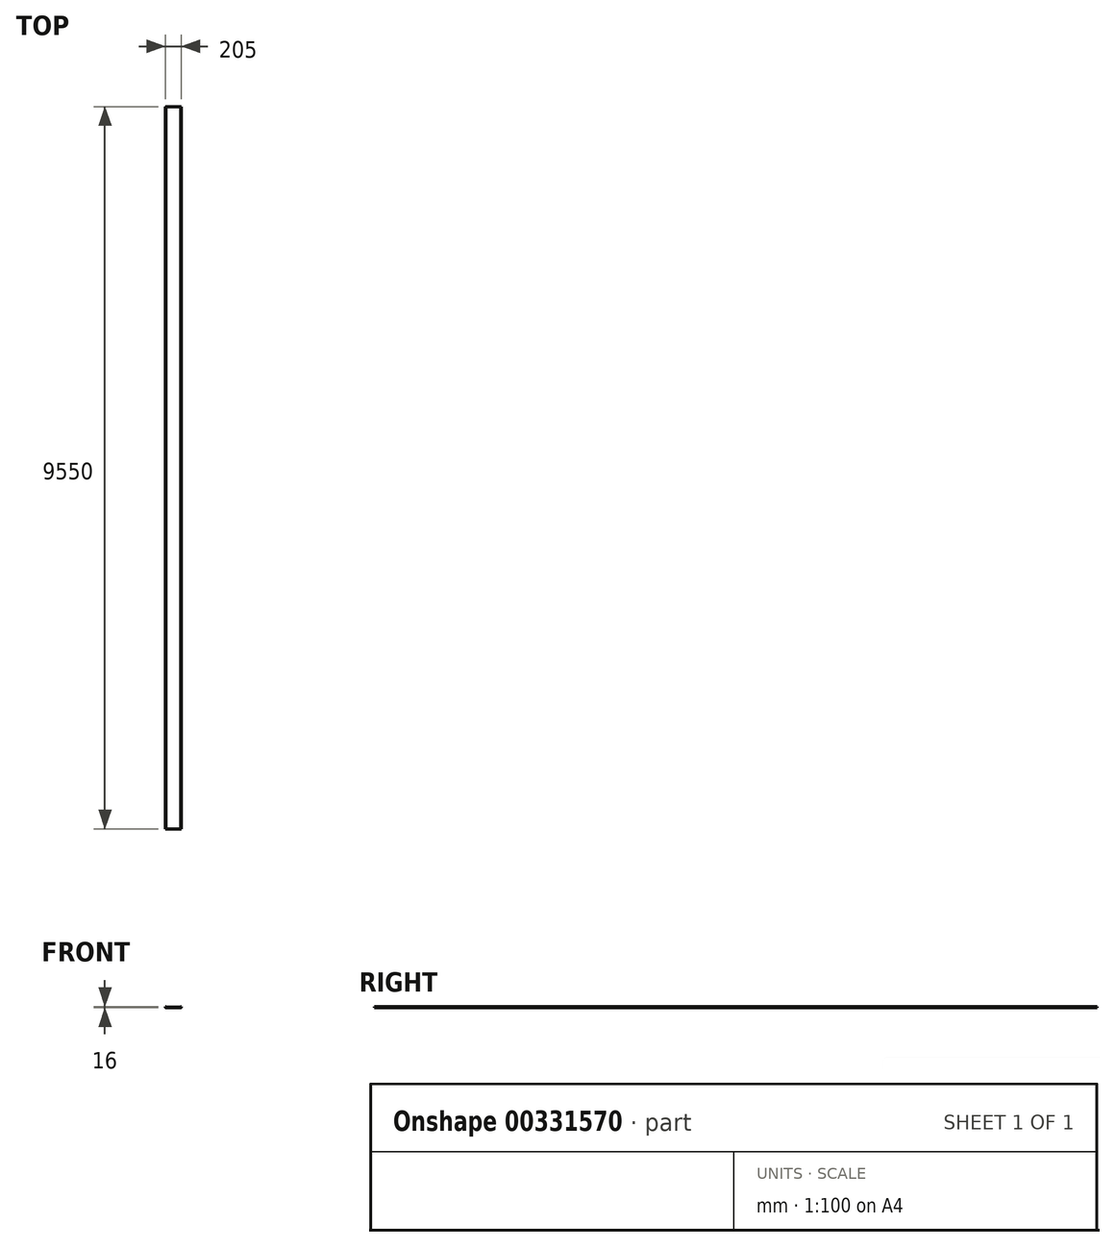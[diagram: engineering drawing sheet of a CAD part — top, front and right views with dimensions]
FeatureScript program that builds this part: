
annotation { "Feature Type Name" : "Feature", "Feature Type Description" : "" }
export const myFeature = defineFeature(function(context is Context, id is Id, definition is map)
    precondition{}
    {
        {
            var Q0;
            Q0=qCreatedBy(makeId("Front.planeOp"),FACE);
            var sketch = newSketch(context, id + "F0", { "sketchPlane" : qUnion([Q0])});
            skLineSegment(sketch, "E0.top", {"start": v(100, -16) * mm, "end": v(-100, -16) * mm});
            skLineSegment(sketch, "E0.left", {"start": v(102.5, 0) * mm, "end": v(102.5, -13.5) * mm});
            skLineSegment(sketch, "E0.right", {"start": v(-102.5, 0) * mm, "end": v(-102.5, -13.5) * mm});
            skPoint(sketch, "E0.middle", {"position": v(0, 0) * mm});
            skLineSegment(sketch, "E1.bottom", {"start": v(94, -10) * mm, "end": v(-94, -10) * mm});
            skLineSegment(sketch, "E1.left", {"start": v(96.5, -7.5) * mm, "end": v(96.5, 0) * mm});
            skLineSegment(sketch, "E1.right", {"start": v(-96.5, -7.5) * mm, "end": v(-96.5, 0) * mm});
            skLineSegment(sketch, "E2.bottom", {"start": v(97, -13) * mm, "end": v(-97, -13) * mm});
            skLineSegment(sketch, "E2.left", {"start": v(99.5, -10.5) * mm, "end": v(99.5, 0) * mm});
            skLineSegment(sketch, "E2.right", {"start": v(-99.5, -10.5) * mm, "end": v(-99.5, 0) * mm});
            skLineSegment(sketch, "E3", {"start": v(-102.5, 0) * mm, "end": v(-96.5, 0) * mm});
            skPoint(sketch, "E4.orphan", {"position": v(-99.5, 13) * mm});
            skPoint(sketch, "E0.bottom.end.orphan", {"position": v(-102.5, 16) * mm});
            skPoint(sketch, "E1.top.end.orphan", {"position": v(-96.5, 10) * mm});
            skPoint(sketch, "E5.orphan", {"position": v(96.5, 10) * mm});
            skPoint(sketch, "E6.orphan", {"position": v(99.5, 13) * mm});
            skPoint(sketch, "E7.orphan", {"position": v(102.5, 16) * mm});
            skLineSegment(sketch, "E8.trimOffspring", {"start": v(96.5, 0) * mm, "end": v(102.5, 0) * mm});
            skPoint(sketch, "E9.visualSharp", {"position": v(102.5, -16) * mm});
            skArc(sketch, "E9.filletArc", {"start": v(100, -16) * mm, "mid": v(101.77, -15.27) * mm, "end": v(102.5, -13.5) * mm});
            skPoint(sketch, "E10.visualSharp", {"position": v(96.5, -10) * mm});
            skArc(sketch, "E10.filletArc", {"start": v(94, -10) * mm, "mid": v(95.77, -9.27) * mm, "end": v(96.5, -7.5) * mm});
            skPoint(sketch, "E11.visualSharp", {"position": v(-96.5, -10) * mm});
            skArc(sketch, "E11.filletArc", {"start": v(-96.5, -7.5) * mm, "mid": v(-95.77, -9.27) * mm, "end": v(-94, -10) * mm});
            skPoint(sketch, "E12.visualSharp", {"position": v(-102.5, -16) * mm});
            skArc(sketch, "E12.filletArc", {"start": v(-102.5, -13.5) * mm, "mid": v(-101.77, -15.27) * mm, "end": v(-100, -16) * mm});
            skPoint(sketch, "E13.visualSharp", {"position": v(-99.5, -13) * mm});
            skArc(sketch, "E13.filletArc", {"start": v(-99.5, -10.5) * mm, "mid": v(-98.77, -12.27) * mm, "end": v(-97, -13) * mm});
            skPoint(sketch, "E14.visualSharp", {"position": v(99.5, -13) * mm});
            skArc(sketch, "E14.filletArc", {"start": v(97, -13) * mm, "mid": v(98.77, -12.27) * mm, "end": v(99.5, -10.5) * mm});
            skSolve(sketch);
        }
        {
            var Q0;
            Q0=qSketchRegion(id+"F0",true);
            extrude(context, id + "F1", {"entities" : qUnion([Q0]), "depth" : 9550 * mm});
        }
    });
